# Revit family: Sink-Wall_Mount-KOHLER-Greenwich-K-2031
name_source: partatom
category: Plumbing Fixtures
revit_build: Autodesk Revit 2015 (Build: 20140606_1530(x64)
units: mm (PartAtom-declared; Revit-internal decimal feet)

## types (6) — shared parameters
ADA Compliant = Yes
Assembly Code = D2010400
CW Connection = No
Cold Water Inlet = Cold Water Inlet
Date Modified = 10/03/2018
Default Elevation = 34"
Drain Included = No
Finish = Kohler-Vitreous_China-0-White
HW Connection = No
Height = 12 7/8"
Hot Water Inlet = Hot Water Inlet
Length = 20 3/4"
Manufacturer = KOHLER Co.
MasterFormat 1995 = 15410
MasterFormat 2004 = 22.41.16
Material = Vitreous China
Product Documentation Link = http://www.us.kohler.com
Product Name = Greenwich
Product Page URL = http://www.us.kohler.com
URL = https://www.us.kohler.com
Vent Connection = No
Waste Connection = Yes
Waste Water Outlet = Waste Water Outlet
Width = 18 1/4"

## per-type parameters (varying)
| type | Description | L | Model | N | NL | NR | O | R | Type |
| Single Faucet Hole, 0 - White | 20-3/4 inch x 18-1/4 inch wall-mount/concealed arm carrier bathroom sink with single faucet hole | No | K-2031-0 | No | No | No | Yes | No | 1 |
| Single Faucet Hole, Left Soap Dispenser, 0 - White | 20-3/4 inch x 18-1/4 inch wall-mount/concealed arm carrier bathroom sink with single faucet hole and left-hand soap dispenser hole | Yes | K-2031-L-0 | No | No | No | No | No | 2 |
| Single Faucet Hole, Right Soap Dispenser, 0 - White | 20-3/4 inch x 18-1/4 inch wall-mount/concealed arm carrier bathroom sink with single faucet hole and right-hand soap dispenser hole | No | K-2031-R-0 | No | No | No | No | Yes | 3 |
| No Overflow, Single Faucet Hole, 0 - White | 20-3/4 inch x 18-1/4 inch wall-mount/concealed arm carrier bathroom sink with single faucet hole and no overflow | No | K-2031-N-0 | Yes | No | No | No | No | 4 |
| No Overflow, Single Faucet Hole, Left Soap Dispenser, 0 - White | 20-3/4 inch x 18-1/4 inch wall-mount/concealed arm carrier bathroom sink with single faucet hole, no overflow and left-hand soap dispenser hole | No | K-2031-NL-0 | No | Yes | No | No | No | 5 |
| No Overflow, Single Faucet Hole, Right Soap Dispenser, 0 - White | 20-3/4 inch x 18-1/4 inch wall-mount/concealed arm carrier bathroom sink with single faucet hole, no overflow and right-hand soap dispenser hole | No | K-2031-NR-0 | No | No | Yes | No | No | 6 |

## geometry (parser evidence)
native form markers: Sweep x5
no freeform markers — native parametric forms only
